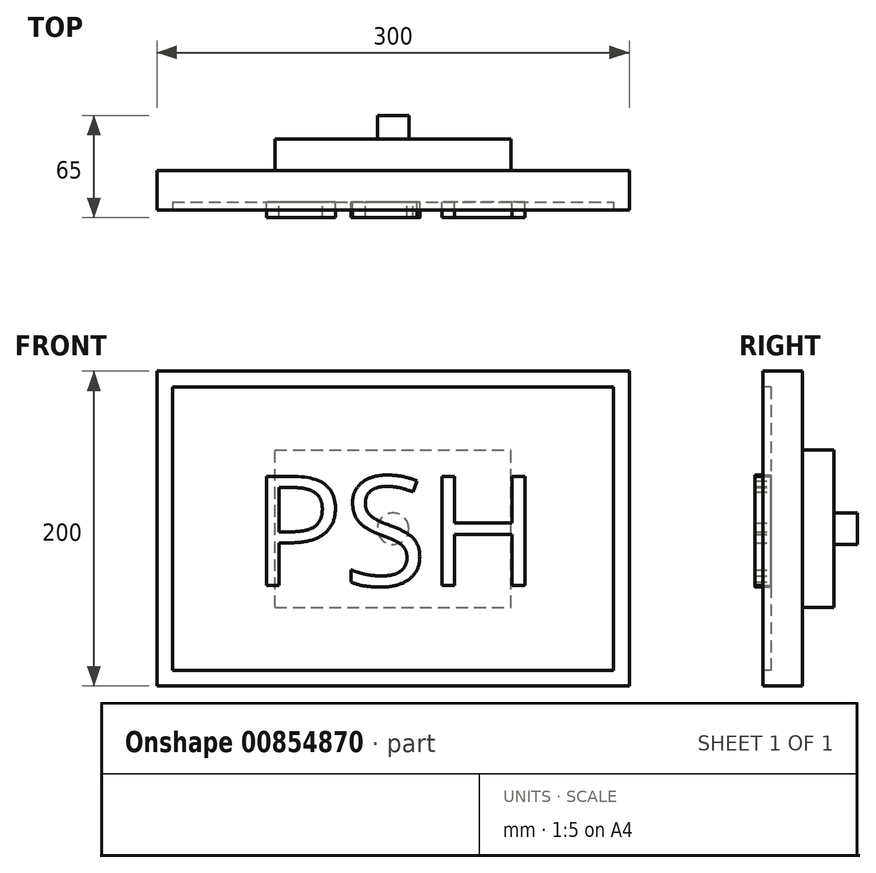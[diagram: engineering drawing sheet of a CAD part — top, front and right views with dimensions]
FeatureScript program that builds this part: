
annotation { "Feature Type Name" : "Feature", "Feature Type Description" : "" }
export const myFeature = defineFeature(function(context is Context, id is Id, definition is map)
    precondition{}
    {
        {
            var Q0;
            Q0=qCreatedBy(makeId("Front.planeOp"),FACE);
            var sketch = newSketch(context, id + "F0", { "sketchPlane" : qUnion([Q0])});
            skLineSegment(sketch, "E0.bottom", {"start": v(-150, 100) * mm, "end": v(150, 100) * mm});
            skLineSegment(sketch, "E0.top", {"start": v(-150, -100) * mm, "end": v(150, -100) * mm});
            skLineSegment(sketch, "E0.left", {"start": v(-150, 100) * mm, "end": v(-150, -100) * mm});
            skLineSegment(sketch, "E0.right", {"start": v(150, 100) * mm, "end": v(150, -100) * mm});
            skSolve(sketch);
        }
        {
            var Q0;
            Q0=makeQuery(id+"F0.imprint","IMPRINT",FACE,{"disambiguationData":[TD([[makeQuery(id+"F0.imprint","IMPRINT",EDGE,{"derivedFrom":sQuery(id+"F0.wireOp",EDGE,"E0.bottom")}),-1.0]])]});
            extrude(context, id + "F1", {"entities" : qUnion([Q0]), "depth" : 25 * mm, "offsetDistance" : 25 * mm});
        }
        {
            var Q0;
            Q0=makeQuery(id+"F1.opExtrude","CAP_FACE",FACE,{"disambiguationData":[OSD([sQuery(id+"F0.wireOp",EDGE,"E0.bottom"),sQuery(id+"F0.wireOp",EDGE,"E0.top"),sQuery(id+"F0.wireOp",EDGE,"E0.left"),sQuery(id+"F0.wireOp",EDGE,"E0.right")])],"isStart":false});
            var sketch = newSketch(context, id + "F2", { "sketchPlane" : qUnion([Q0])});
            skLineSegment(sketch, "E1.bottom", {"start": v(-140, 90) * mm, "end": v(140, 90) * mm});
            skLineSegment(sketch, "E1.top", {"start": v(-140, -90) * mm, "end": v(140, -90) * mm});
            skLineSegment(sketch, "E1.left", {"start": v(-140, 90) * mm, "end": v(-140, -90) * mm});
            skLineSegment(sketch, "E1.right", {"start": v(140, 90) * mm, "end": v(140, -90) * mm});
            skSolve(sketch);
        }
        {
            var Q0;
            Q0 = qSketchRegion(id + "F2", true);
            extrude(context, id + "F3", {"entities" : qUnion([Q0]), "operationType" : NewBodyOperationType.REMOVE, "oppositeDirection" : true, "depth" : 5 * mm, "offsetDistance" : 25 * mm});
        }
        {
            var Q0;
            Q0=makeQuery(id+"F1.opExtrude","CAP_FACE",FACE,{"disambiguationData":[OSD([sQuery(id+"F0.wireOp",EDGE,"E0.bottom"),sQuery(id+"F0.wireOp",EDGE,"E0.top"),sQuery(id+"F0.wireOp",EDGE,"E0.left"),sQuery(id+"F0.wireOp",EDGE,"E0.right")])],"isStart":true});
            var sketch = newSketch(context, id + "F4", { "sketchPlane" : qUnion([Q0])});
            skLineSegment(sketch, "E2.bottom", {"start": v(75, -50) * mm, "end": v(-75, -50) * mm});
            skLineSegment(sketch, "E2.top", {"start": v(75, 50) * mm, "end": v(-75, 50) * mm});
            skLineSegment(sketch, "E2.left", {"start": v(75, -50) * mm, "end": v(75, 50) * mm});
            skLineSegment(sketch, "E2.right", {"start": v(-75, -50) * mm, "end": v(-75, 50) * mm});
            skPoint(sketch, "E2.middle", {"position": v(0, 0) * mm});
            skSolve(sketch);
        }
        {
            var Q0;
            Q0=makeQuery(id+"F4.imprint","IMPRINT",FACE,{"disambiguationData":[TD([[makeQuery(id+"F4.imprint","IMPRINT",EDGE,{"derivedFrom":sQuery(id+"F4.wireOp",EDGE,"E2.bottom")}),-1.0]])]});
            extrude(context, id + "F5", {"entities" : qUnion([Q0]), "operationType" : NewBodyOperationType.ADD, "depth" : 20 * mm, "offsetDistance" : 25 * mm});
        }
        {
            var Q0;
            Q0=makeQuery(id+"F5.opExtrude","CAP_FACE",FACE,{"disambiguationData":[OSD([sQuery(id+"F4.wireOp",EDGE,"E2.bottom"),sQuery(id+"F4.wireOp",EDGE,"E2.top"),sQuery(id+"F4.wireOp",EDGE,"E2.left"),sQuery(id+"F4.wireOp",EDGE,"E2.right")])],"isStart":false});
            var sketch = newSketch(context, id + "F6", { "sketchPlane" : qUnion([Q0])});
            skCircle(sketch, "E3", {"center": v(0, 0) * mm, "radius": 10 * mm});
            skSolve(sketch);
        }
        {
            var Q0;
            Q0=makeQuery(id+"F6.imprint","IMPRINT",FACE,{"disambiguationData":[TD([[makeQuery(id+"F6.imprint","IMPRINT",EDGE,{"derivedFrom":sQuery(id+"F6.wireOp",EDGE,"E3")}),1.0]])]});
            extrude(context, id + "F7", {"entities" : qUnion([Q0]), "operationType" : NewBodyOperationType.ADD, "depth" : 15 * mm, "offsetDistance" : 25 * mm});
        }
        {
            var Q0;
            Q0=makeQuery(id+"F3.boolean.opBoolean","COPY",FACE,{"derivedFrom":makeQuery(id+"F3.opExtrude","CAP_FACE",FACE,{"disambiguationData":[OSD([sQuery(id+"F2.wireOp",EDGE,"E1.bottom"),sQuery(id+"F2.wireOp",EDGE,"E1.top"),sQuery(id+"F2.wireOp",EDGE,"E1.left"),sQuery(id+"F2.wireOp",EDGE,"E1.right")])],"isStart":false})});
            var sketch = newSketch(context, id + "F8", { "sketchPlane" : qUnion([Q0])});
            skText(sketch, "E4", { "text": "PSH", "fontName": "OpenSans-Regular.ttf"});
            const initialGuessF8  = {"E4": [-0.09, -0.03616, 1, 0, 0.06983]};
            skSetInitialGuess(sketch, initialGuessF8);
            skSolve(sketch);
        }
        {
            var Q0;
            Q0 = qSketchRegion(id + "F8", true);
            extrude(context, id + "F9", {"entities" : qUnion([Q0]), "operationType" : NewBodyOperationType.ADD, "depth" : 10 * mm, "offsetDistance" : 25 * mm});
        }
    });
